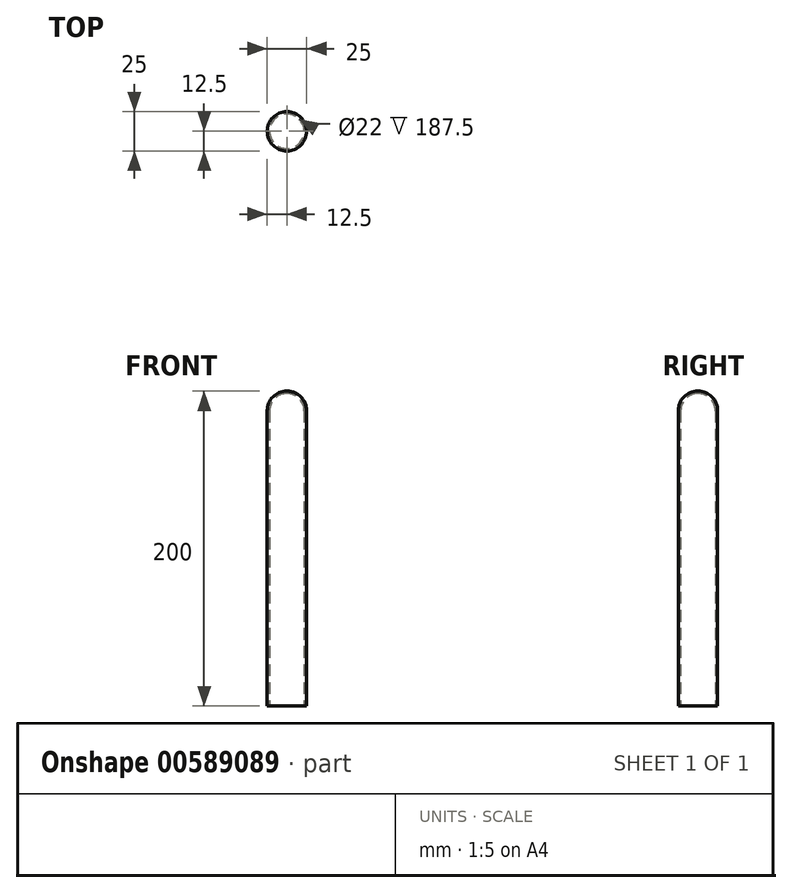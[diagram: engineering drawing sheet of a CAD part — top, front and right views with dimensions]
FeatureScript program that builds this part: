
annotation { "Feature Type Name" : "Feature", "Feature Type Description" : "" }
export const myFeature = defineFeature(function(context is Context, id is Id, definition is map)
    precondition{}
    {
        {
            var Q0;
            Q0=qCreatedBy(makeId("Top.planeOp"),FACE);
            var sketch = newSketch(context, id + "F0", { "sketchPlane" : qUnion([Q0])});
            skCircle(sketch, "E0", {"center": v(0, 0) * mm, "radius": 12.5 * mm});
            skCircle(sketch, "E1", {"center": v(0, 0) * mm, "radius": 11 * mm});
            skSolve(sketch);
        }
        {
            var Q0;
            Q0 = qSketchRegion(id + "F0", true);
            extrude(context, id + "F1", {"entities" : qUnion([Q0]), "depth" : 187.5 * mm, "offsetDistance" : 25 * mm});
        }
        {
            var Q0;
            Q0=qCreatedBy(makeId("Front.planeOp"),FACE);
            var sketch = newSketch(context, id + "F2", { "sketchPlane" : qUnion([Q0])});
            skLineSegment(sketch, "E2", {"start": v(0, 187.5) * mm, "end": v(-11, 187.5) * mm, "construction": true});
            skArc(sketch, "E3", {"start": v(-12.5, 187.5) * mm, "mid": v(-8.84, 196.34) * mm, "end": v(0, 200) * mm});
            skArc(sketch, "E4", {"start": v(0, 198.5) * mm, "mid": v(-7.78, 195.28) * mm, "end": v(-11, 187.5) * mm});
            skLineSegment(sketch, "E5", {"start": v(0, 187.5) * mm, "end": v(0, 200) * mm, "construction": true});
            skLineSegment(sketch, "E6", {"start": v(-12.5, 187.5) * mm, "end": v(-11, 187.5) * mm});
            skLineSegment(sketch, "E7", {"start": v(0, 198.5) * mm, "end": v(0, 200) * mm});
            skSolve(sketch);
        }
        {
            var Q0;
            Q0 = qSketchRegion(id + "F2", true);
            var Q1;
            Q1=sQuery(id+"F2.wireOp",EDGE,"E5");
            revolve(context, id + "F3", {"operationType" : NewBodyOperationType.ADD, "entities" : qUnion([Q0]), "axis" : qUnion([Q1]), "revolveType" : RevolveType.FULL, "oppositeDirection" : true});
        }
    });
